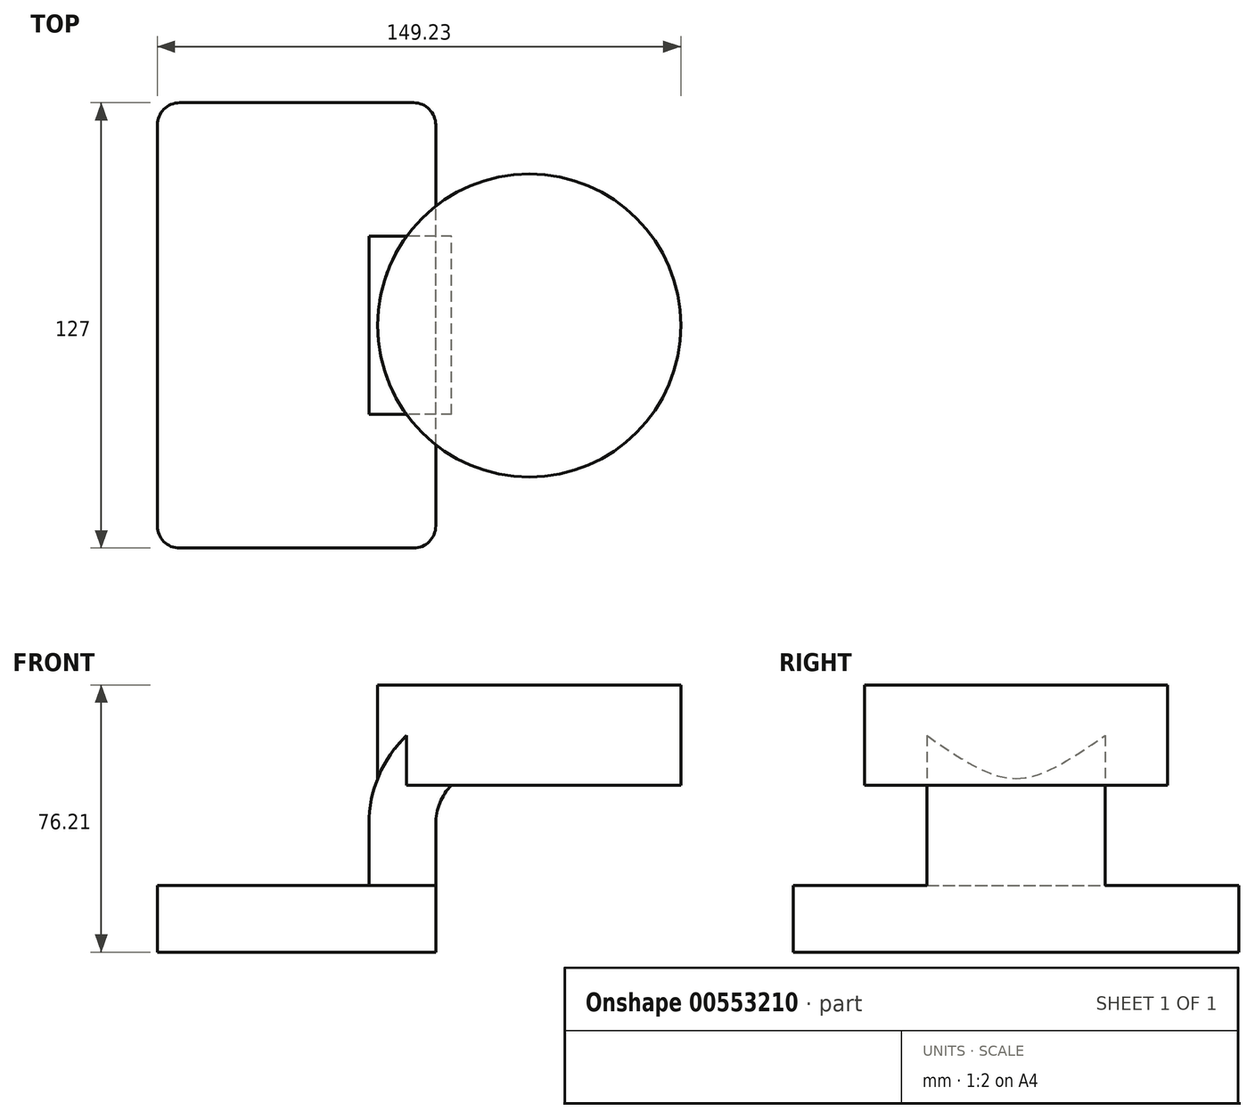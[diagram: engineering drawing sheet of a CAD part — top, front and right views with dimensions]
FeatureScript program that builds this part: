
annotation { "Feature Type Name" : "Feature", "Feature Type Description" : "" }
export const myFeature = defineFeature(function(context is Context, id is Id, definition is map)
    precondition{}
    {
        {
            var Q0;
            Q0=qCreatedBy(makeId("Front.planeOp"),FACE);
            var sketch = newSketch(context, id + "F0", { "sketchPlane" : qUnion([Q0])});
            skLineSegment(sketch, "E0.bottom", {"start": v(39.69, 9.53) * mm, "end": v(-39.69, 9.53) * mm});
            skLineSegment(sketch, "E0.top", {"start": v(39.69, -9.52) * mm, "end": v(-39.69, -9.52) * mm});
            skLineSegment(sketch, "E0.left", {"start": v(39.69, 9.53) * mm, "end": v(39.69, -9.52) * mm});
            skLineSegment(sketch, "E0.right", {"start": v(-39.69, 9.53) * mm, "end": v(-39.69, -9.52) * mm});
            skPoint(sketch, "E0.middle", {"position": v(0, 0) * mm});
            skLineSegment(sketch, "E1.bottom", {"start": v(109.54, 38.1) * mm, "end": v(58.74, 38.1) * mm});
            skLineSegment(sketch, "E1.top", {"start": v(109.54, 66.68) * mm, "end": v(58.74, 66.68) * mm});
            skLineSegment(sketch, "E1.left", {"start": v(109.54, 38.1) * mm, "end": v(109.54, 66.68) * mm});
            skLineSegment(sketch, "E1.right", {"start": v(58.74, 38.1) * mm, "end": v(58.74, 66.68) * mm});
            skPoint(sketch, "E1.middle", {"position": v(84.14, 52.39) * mm});
            skLineSegment(sketch, "E2", {"start": v(39.69, 9.53) * mm, "end": v(39.69, 27.03) * mm});
            skArc(sketch, "E3", {"start": v(39.69, 27.03) * mm, "mid": v(44.34, 38.25) * mm, "end": v(55.56, 42.9) * mm});
            skLineSegment(sketch, "E4", {"start": v(55.56, 42.9) * mm, "end": v(66.18, 42.9) * mm});
            skLineSegment(sketch, "E5.0", {"start": v(55.56, 61.95) * mm, "end": v(66.18, 61.95) * mm});
            skArc(sketch, "E5.1", {"start": v(20.64, 27.03) * mm, "mid": v(30.87, 51.72) * mm, "end": v(55.56, 61.95) * mm});
            skLineSegment(sketch, "E5.2", {"start": v(20.64, 9.53) * mm, "end": v(20.64, 27.03) * mm});
            skLineSegment(sketch, "E6", {"start": v(66.33, 38.1) * mm, "end": v(66.33, 66.68) * mm});
            skFitSpline(sketch, "E7", {"points": [v(-39.69, 9.52) * mm, v(58.74, 61.95) * mm], "startDerivative": vector(42.42, 134.12) * mm, "endDerivative": vector(127.8, -10.46) * mm});
            skSolve(sketch);
        }
        {
            var Q0;
            Q0=makeQuery(id+"F0.imprint","IMPRINT",FACE,{"disambiguationData":[TD([[makeQuery(id+"F0.imprint","IMPRINT",EDGE,{"derivedFrom":sQuery(id+"F0.wireOp",EDGE,"E0.top")}),-1.0]])]});
            extrude(context, id + "F1", {"entities" : qUnion([Q0]), "endBound" : BoundingType.SYMMETRIC, "depth" : 127 * mm, "offsetDistance" : 25.4 * mm});
        }
        {
            var Q0;
            {var subQ1=sQuery(id+"F0.wireOp",EDGE,"E2");Q0=makeQuery(id+"F0.imprint","IMPRINT",FACE,{"disambiguationData":[TD([[makeQuery(id+"F0.imprint","IMPRINT",EDGE,{"derivedFrom":subQ1}),1.0]])]});}
            var Q1;
            {var subQ6=sQuery(id+"F0.wireOp",EDGE,"E6");Q1=makeQuery(id+"F0.imprint","IMPRINT",FACE,{"disambiguationData":[TD([[makeQuery(id+"F0.imprint","IMPRINT",EDGE,{"derivedFrom":subQ6}),1.0]])]});}
            extrude(context, id + "F2", {"entities" : qUnion([Q0, Q1]), "operationType" : NewBodyOperationType.ADD, "endBound" : BoundingType.SYMMETRIC, "depth" : 50.8 * mm, "offsetDistance" : 25.4 * mm});
        }
        {
            var Q0;
            {var subQ1=sQuery(id+"F0.wireOp",EDGE,"E5.1");Q0=makeQuery(id+"F0.imprint","IMPRINT",FACE,{"disambiguationData":[TD([[makeQuery(id+"F0.imprint","IMPRINT",EDGE,{"derivedFrom":subQ1}),1.0]])]});}
            extrude(context, id + "F3", {"entities" : qUnion([Q0]), "operationType" : NewBodyOperationType.ADD, "endBound" : BoundingType.SYMMETRIC, "depth" : 15.88 * mm, "offsetDistance" : 25.4 * mm});
        }
        {
            var Q0;
            {var subQ0=sQuery(id+"F0.wireOp",EDGE,"E1.left");Q0=makeQuery(id+"F0.imprint","IMPRINT",FACE,{"disambiguationData":[TD([[makeQuery(id+"F0.imprint","IMPRINT",EDGE,{"derivedFrom":subQ0}),1.0]])]});}
            var Q1;
            Q1=sQuery(id+"F0.wireOp",EDGE,"E6");
            revolve(context, id + "F4", {"operationType" : NewBodyOperationType.ADD, "entities" : qUnion([Q0]), "axis" : qUnion([Q1]), "revolveType" : RevolveType.FULL});
        }
        {
            var Q0;
            Q0=makeQuery(id+"F1.opExtrude","CAP_EDGE",EDGE,{"disambiguationData":[OSD([sQuery(id+"F0.wireOp",EDGE,"E0.left")])],"isStart":false});
            var Q1;
            Q1=makeQuery(id+"F1.opExtrude","CAP_EDGE",EDGE,{"disambiguationData":[OSD([sQuery(id+"F0.wireOp",EDGE,"E0.right")])],"isStart":false});
            var Q2;
            Q2=makeQuery(id+"F1.opExtrude","CAP_EDGE",EDGE,{"disambiguationData":[OSD([sQuery(id+"F0.wireOp",EDGE,"E0.left")])],"isStart":true});
            var Q3;
            Q3=makeQuery(id+"F1.opExtrude","CAP_EDGE",EDGE,{"disambiguationData":[OSD([sQuery(id+"F0.wireOp",EDGE,"E0.right")])],"isStart":true});
            fillet(context, id + "F5", {"entities" : qUnion([Q0, Q1, Q2, Q3]), "radius" : 6.35 * mm, "tangentPropagation" : true, "allowEdgeOverflow" : false});
        }
    });
